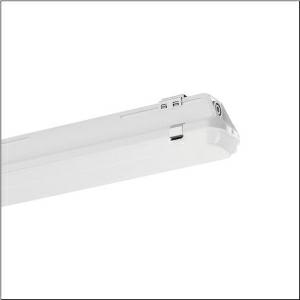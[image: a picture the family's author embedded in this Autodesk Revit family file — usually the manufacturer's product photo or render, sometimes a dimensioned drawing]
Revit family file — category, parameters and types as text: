
# Revit family: monsun_11_51fp207p460h
name_source: partatom
category: Lighting Fixtures
units: mm (PartAtom-declared; Revit-internal decimal feet)

## family parameters
Cut with Voids When Loaded = No
Host = Face
Light Source = No
Part Type = Normal
Room Calculation Point = No
Round Connector Dimension = Use Diameter
Shared = No

## types (1)
- Monsun 11 (1 x LED, 6030 lm, 37.7 W, 4000K)
    Apparent Load = 38 VA
    CIE Flux Codes = 45 75 93 94 100
    Color Rendering = 80
    Color Temperature = 4000K
    Default Elevation = 1800 mm
    Description = Monsun 11, damp-proof luminaire, chain hanger, primary optical cover: enclosure, of PC, light emission: direct distribution, primary light characteristic: symmetric, installation type: suspended mounting, surface-mounted, horizontal mounting, vertical mounting, LED, rated luminous flux: 6.030lm, luminous efficacy: 160lm/W, light colour: 840, colour temperature: 4000K, control gear: ON/OFF, with terminal, 3-pole, max. 2.5mm², mains connection: 220..240V, AC, 50/60Hz, rated input power: 38W, luminaire housing, of glass-fibre reinforced polyester, uncoated, bright grey, incl. chain hanger, length: 1.590mm, width: 90mm, height: 88mm, clip for enclosure, of stainless steel (V2A), ceiling mounting element, of stainless steel (V2A), chain hanger, of stainless steel (V2A), protection rating (complete): IP66, insulation class (complete): insulation class I (protective earthing), certification: CE, ENEC, VDE, UKCA, protection symbol: D, impact resistance: IK08, permissible operating ambient temperature: -35..+40°C, standard: EN 50419, EN 60598-2-1, no direct snow, no direct sun, no direct rain, for indoor or canopied outdoor use, corresponds to IFS (International Featured Standards) requirements for safety and quality in the food industry, contact your sales advisor before using the luminaires in applications with unclear chemical exposure, large temperature fluctuations or condensation-forming humidity, LABS conformity tested according to VDMA 24364:2018-05, packaging unit: 1 piece
    Height = 89 mm
    Lamp = 1 x LED
    Lamp Light Flux = 6030 lm
    Lamp Power = 37.7 W
    Lamp count = 1
    Length = 1590 mm
    Luminous efficacy = 160 lm/W
    Manufacturer = Siteco
    ModVariant = No
    Model = 51FP207P460H
    Mounting Place = Ceiling
    Mounting Type = Surface mounted
    Number of Poles = 1
    OnlyDefault = Yes
    Power Factor = 1
    Product Name = Monsun 11
    Product group = damp-proof luminaire
    ProductGroupID = 300
    Protection Class = Protection class I
    Protection Degree = IP 66
    RLX_Detail_Level = 1
    RLX_Emergency_Light_Flux = 0 lm
    RLX_Emergency_Type = 0
    RLX_Emergency_Type_DB = No
    RlxData = <blob elided: 88645 chars, md5=26206594>
    Socket = socket
    Standby Power = 0 W
    System Light Flux = 6030 lm
    System Power = 38 W
    Type Comments = Product without accessories
    Type Image = l_1349237.jpg
    URL = http://relux.com
    VarID = ---
    Voltage = 0 V
    Weight = 0.00 kg
    Width = 90 mm

## geometry (parser evidence)
native form markers: Blend x4, Sweep x13
no freeform markers — native parametric forms only
